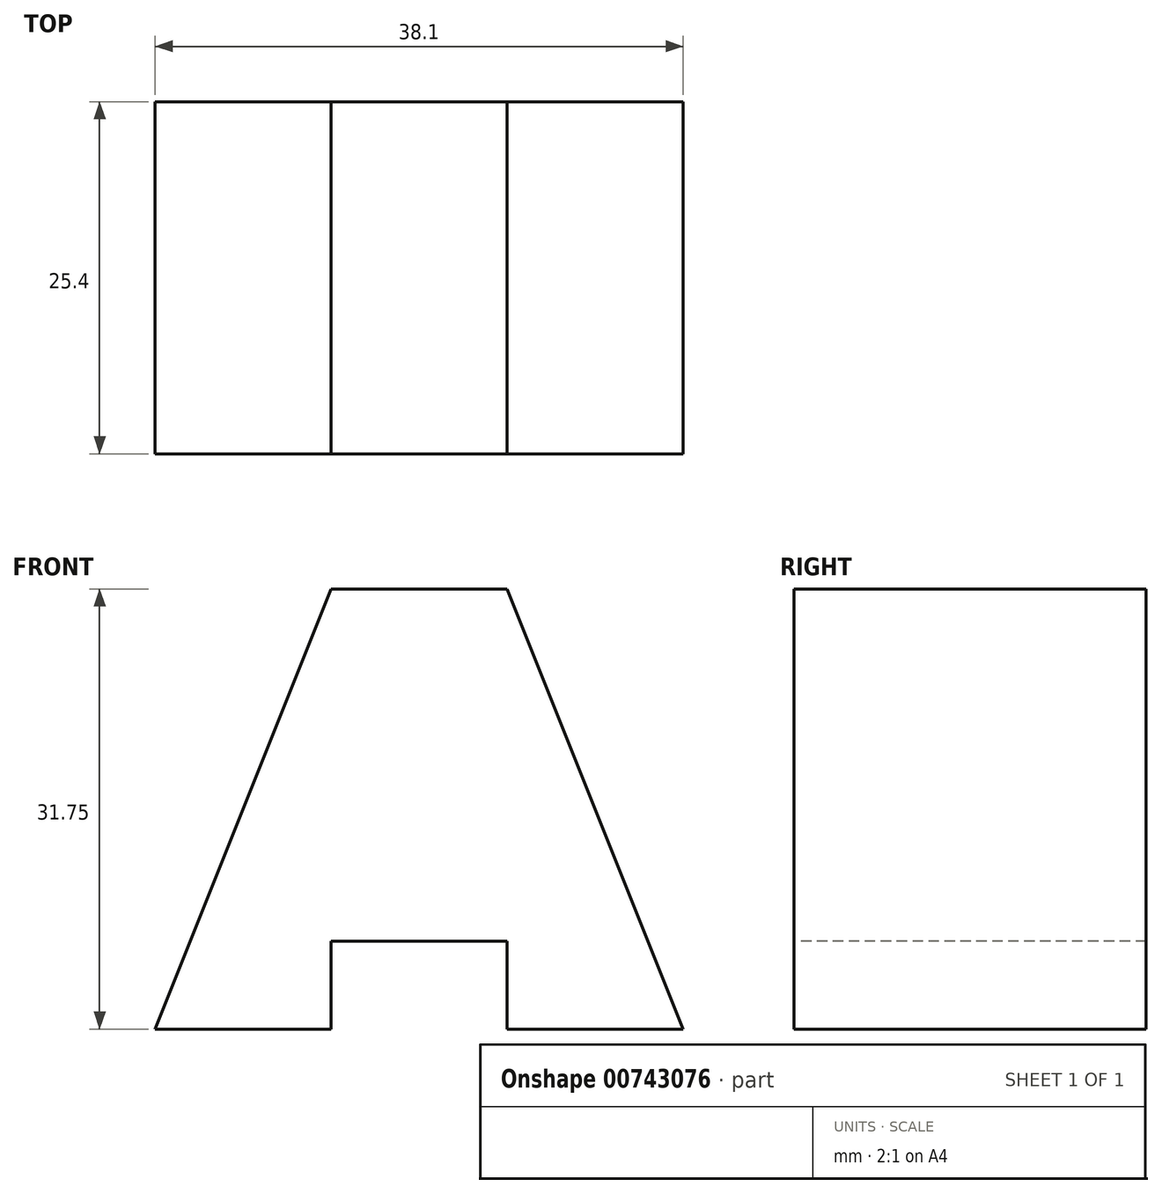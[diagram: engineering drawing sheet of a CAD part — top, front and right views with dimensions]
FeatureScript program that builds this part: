
annotation { "Feature Type Name" : "Feature", "Feature Type Description" : "" }
export const myFeature = defineFeature(function(context is Context, id is Id, definition is map)
    precondition{}
    {
        {
            var Q0;
            Q0=qCreatedBy(makeId("Front.planeOp"),FACE);
            var sketch = newSketch(context, id + "F0", { "sketchPlane" : qUnion([Q0])});
            skLineSegment(sketch, "E0", {"start": v(0, 0) * mm, "end": v(38.1, 0) * mm});
            skLineSegment(sketch, "E1", {"start": v(38.1, 0) * mm, "end": v(38.1, 31.75) * mm});
            skLineSegment(sketch, "E2", {"start": v(38.1, 31.75) * mm, "end": v(0, 31.75) * mm});
            skLineSegment(sketch, "E3", {"start": v(0, 31.75) * mm, "end": v(0, 0) * mm});
            skSolve(sketch);
        }
        {
            var Q0;
            Q0=makeQuery(id+"F0.imprint","IMPRINT",FACE,{"disambiguationData":[TD([[makeQuery(id+"F0.imprint","IMPRINT",EDGE,{"derivedFrom":sQuery(id+"F0.wireOp",EDGE,"E0")}),1.0]])]});
            extrude(context, id + "F1", {"entities" : qUnion([Q0]), "depth" : 25.4 * mm, "offsetDistance" : 25.4 * mm});
        }
        {
            var Q0;
            Q0=makeQuery(id+"F1.opExtrude","CAP_FACE",FACE,{"disambiguationData":[OSD([sQuery(id+"F0.wireOp",EDGE,"E0"),sQuery(id+"F0.wireOp",EDGE,"E1"),sQuery(id+"F0.wireOp",EDGE,"E2"),sQuery(id+"F0.wireOp",EDGE,"E3")])],"isStart":false});
            var sketch = newSketch(context, id + "F2", { "sketchPlane" : qUnion([Q0])});
            skLineSegment(sketch, "E4", {"start": v(25.4, 31.75) * mm, "end": v(38.1, 0) * mm});
            skSolve(sketch);
        }
        {
            var Q0;
            {var subQ0=sQuery(id+"F2.wireOp",EDGE,"E4");Q0=makeQuery(id+"F2.imprint","IMPRINT",FACE,{"disambiguationData":[TD([[makeQuery(id+"F2.imprint","IMPRINT",EDGE,{"derivedFrom":subQ0}),-1.0]])]});}
            var sketch = newSketch(context, id + "F3", { "sketchPlane" : qUnion([Q0])});
            skLineSegment(sketch, "E5", {"start": v(12.7, 31.79) * mm, "end": v(0, 0) * mm});
            skSolve(sketch);
        }
        {
            var Q0;
            {var subQ0=sQuery(id+"F2.wireOp",EDGE,"E4");Q0=makeQuery(id+"F2.imprint","IMPRINT",FACE,{"disambiguationData":[TD([[makeQuery(id+"F2.imprint","IMPRINT",EDGE,{"derivedFrom":subQ0}),1.0]])]});}
            extrude(context, id + "F4", {"entities" : qUnion([Q0]), "operationType" : NewBodyOperationType.REMOVE, "oppositeDirection" : true, "depth" : 25.4 * mm, "offsetDistance" : 25.4 * mm});
        }
        {
            var Q0;
            {var subQ1=makeQuery(id+"F1.opExtrude","CAP_EDGE",EDGE,{"disambiguationData":[OSD([sQuery(id+"F0.wireOp",EDGE,"E3")])],"isStart":false});var subQ2=makeQuery(id+"F2.imprint","IMPRINT",EDGE,{"derivedFrom":subQ1});Q0=makeQuery(id+"F3.imprint","IMPRINT",FACE,{"disambiguationData":[TD([[makeQuery(id+"F3.imprint","IMPRINT",EDGE,{"derivedFrom":subQ2}),1.0]])]});}
            extrude(context, id + "F5", {"entities" : qUnion([Q0]), "operationType" : NewBodyOperationType.REMOVE, "oppositeDirection" : true, "depth" : 25.4 * mm, "offsetDistance" : 25.4 * mm});
        }
        {
            var Q0;
            Q0=makeQuery(id+"F1.opExtrude","CAP_FACE",FACE,{"disambiguationData":[OSD([sQuery(id+"F0.wireOp",EDGE,"E0"),sQuery(id+"F0.wireOp",EDGE,"E1"),sQuery(id+"F0.wireOp",EDGE,"E2"),sQuery(id+"F0.wireOp",EDGE,"E3")])],"isStart":false});
            var sketch = newSketch(context, id + "F6", { "sketchPlane" : qUnion([Q0])});
            skLineSegment(sketch, "E6", {"start": v(12.7, 0) * mm, "end": v(12.7, 6.35) * mm});
            skLineSegment(sketch, "E7", {"start": v(12.7, 6.35) * mm, "end": v(25.4, 6.35) * mm});
            skLineSegment(sketch, "E8", {"start": v(25.4, 6.35) * mm, "end": v(25.4, 0) * mm});
            skLineSegment(sketch, "E9", {"start": v(25.4, 0) * mm, "end": v(12.7, 0) * mm});
            skSolve(sketch);
        }
        {
            var Q0;
            Q0=makeQuery(id+"F6.imprint","IMPRINT",FACE,{"disambiguationData":[TD([[makeQuery(id+"F6.imprint","IMPRINT",EDGE,{"derivedFrom":sQuery(id+"F6.wireOp",EDGE,"E6")}),-1.0]])]});
            extrude(context, id + "F7", {"entities" : qUnion([Q0]), "operationType" : NewBodyOperationType.REMOVE, "oppositeDirection" : true, "depth" : 25.4 * mm, "offsetDistance" : 25.4 * mm});
        }
    });
